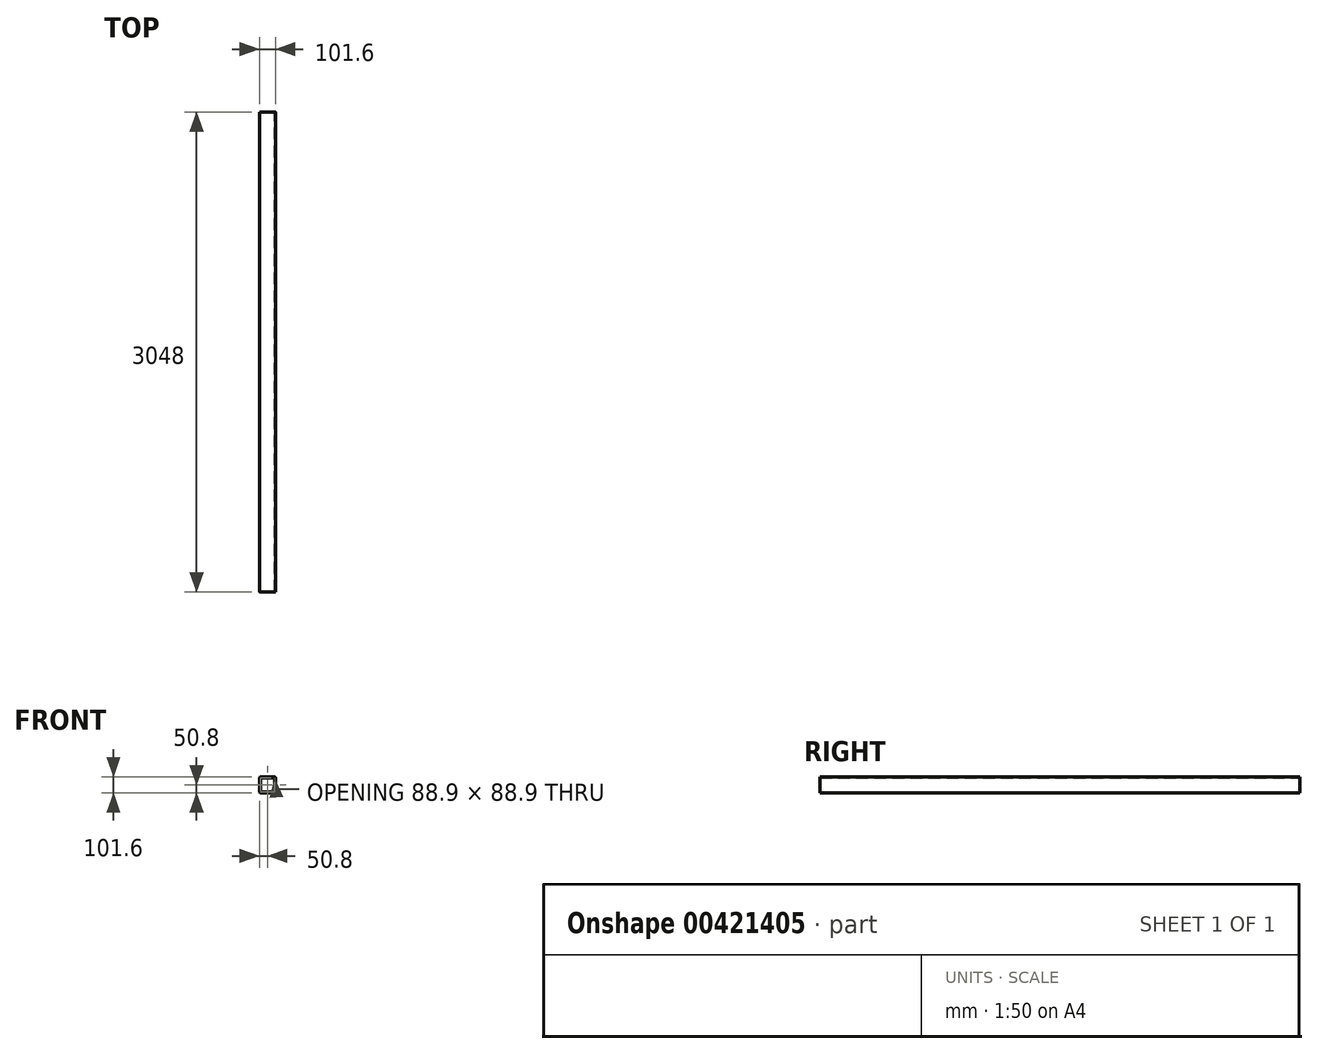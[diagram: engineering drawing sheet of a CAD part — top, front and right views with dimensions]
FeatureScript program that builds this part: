
annotation { "Feature Type Name" : "Feature", "Feature Type Description" : "" }
export const myFeature = defineFeature(function(context is Context, id is Id, definition is map)
    precondition{}
    {
        {
            var Q0;
            Q0=qCreatedBy(makeId("Front.planeOp"),FACE);
            var sketch = newSketch(context, id + "F0", { "sketchPlane" : qUnion([Q0])});
            skLineSegment(sketch, "E0.bottom", {"start": v(44.45, -44.45) * mm, "end": v(-44.45, -44.45) * mm});
            skLineSegment(sketch, "E0.top", {"start": v(44.45, 44.45) * mm, "end": v(-44.45, 44.45) * mm});
            skLineSegment(sketch, "E0.left", {"start": v(44.45, -44.45) * mm, "end": v(44.45, 44.45) * mm});
            skLineSegment(sketch, "E0.right", {"start": v(-44.45, -44.45) * mm, "end": v(-44.45, 44.45) * mm});
            skPoint(sketch, "E0.middle", {"position": v(0, 0) * mm});
            skLineSegment(sketch, "E1.bottom", {"start": v(50.8, -50.8) * mm, "end": v(-50.8, -50.8) * mm});
            skLineSegment(sketch, "E1.top", {"start": v(50.8, 50.8) * mm, "end": v(-50.8, 50.8) * mm});
            skLineSegment(sketch, "E1.left", {"start": v(50.8, -50.8) * mm, "end": v(50.8, 50.8) * mm});
            skLineSegment(sketch, "E1.right", {"start": v(-50.8, -50.8) * mm, "end": v(-50.8, 50.8) * mm});
            skSolve(sketch);
        }
        {
            var Q0;
            Q0 = qSketchRegion(id + "F0", true);
            extrude(context, id + "F1", {"entities" : qUnion([Q0]), "endBound" : BoundingType.SYMMETRIC, "depth" : 3048 * mm});
        }
        {
            var Q0;
            Q0=makeQuery(id+"F1.opExtrude","SWEPT_EDGE",EDGE,{"disambiguationData":[OSD([sQuery(id+"F0.wireOp",EDGE,"E1.top"),sQuery(id+"F0.wireOp",EDGE,"E1.right")])]});
            var Q1;
            Q1=makeQuery(id+"F1.opExtrude","SWEPT_EDGE",EDGE,{"disambiguationData":[OSD([sQuery(id+"F0.wireOp",EDGE,"E1.bottom"),sQuery(id+"F0.wireOp",EDGE,"E1.right")])]});
            var Q2;
            Q2=makeQuery(id+"F1.opExtrude","SWEPT_EDGE",EDGE,{"disambiguationData":[OSD([sQuery(id+"F0.wireOp",EDGE,"E1.top"),sQuery(id+"F0.wireOp",EDGE,"E1.left")])]});
            var Q3;
            Q3=makeQuery(id+"F1.opExtrude","SWEPT_EDGE",EDGE,{"disambiguationData":[OSD([sQuery(id+"F0.wireOp",EDGE,"E1.bottom"),sQuery(id+"F0.wireOp",EDGE,"E1.left")])]});
            var Q4;
            Q4=makeQuery(id+"F1.opExtrude","SWEPT_EDGE",EDGE,{"disambiguationData":[OSD([sQuery(id+"F0.wireOp",EDGE,"E0.bottom"),sQuery(id+"F0.wireOp",EDGE,"E0.right")])]});
            var Q5;
            Q5=makeQuery(id+"F1.opExtrude","SWEPT_EDGE",EDGE,{"disambiguationData":[OSD([sQuery(id+"F0.wireOp",EDGE,"E0.top"),sQuery(id+"F0.wireOp",EDGE,"E0.right")])]});
            var Q6;
            Q6=makeQuery(id+"F1.opExtrude","SWEPT_EDGE",EDGE,{"disambiguationData":[OSD([sQuery(id+"F0.wireOp",EDGE,"E0.bottom"),sQuery(id+"F0.wireOp",EDGE,"E0.left")])]});
            var Q7;
            Q7=makeQuery(id+"F1.opExtrude","SWEPT_EDGE",EDGE,{"disambiguationData":[OSD([sQuery(id+"F0.wireOp",EDGE,"E0.top"),sQuery(id+"F0.wireOp",EDGE,"E0.left")])]});
            fillet(context, id + "F2", {"entities" : qUnion([Q0, Q1, Q2, Q3, Q4, Q5, Q6, Q7]), "radius" : 6.35 * mm, "tangentPropagation" : true, "allowEdgeOverflow" : false});
        }
    });
